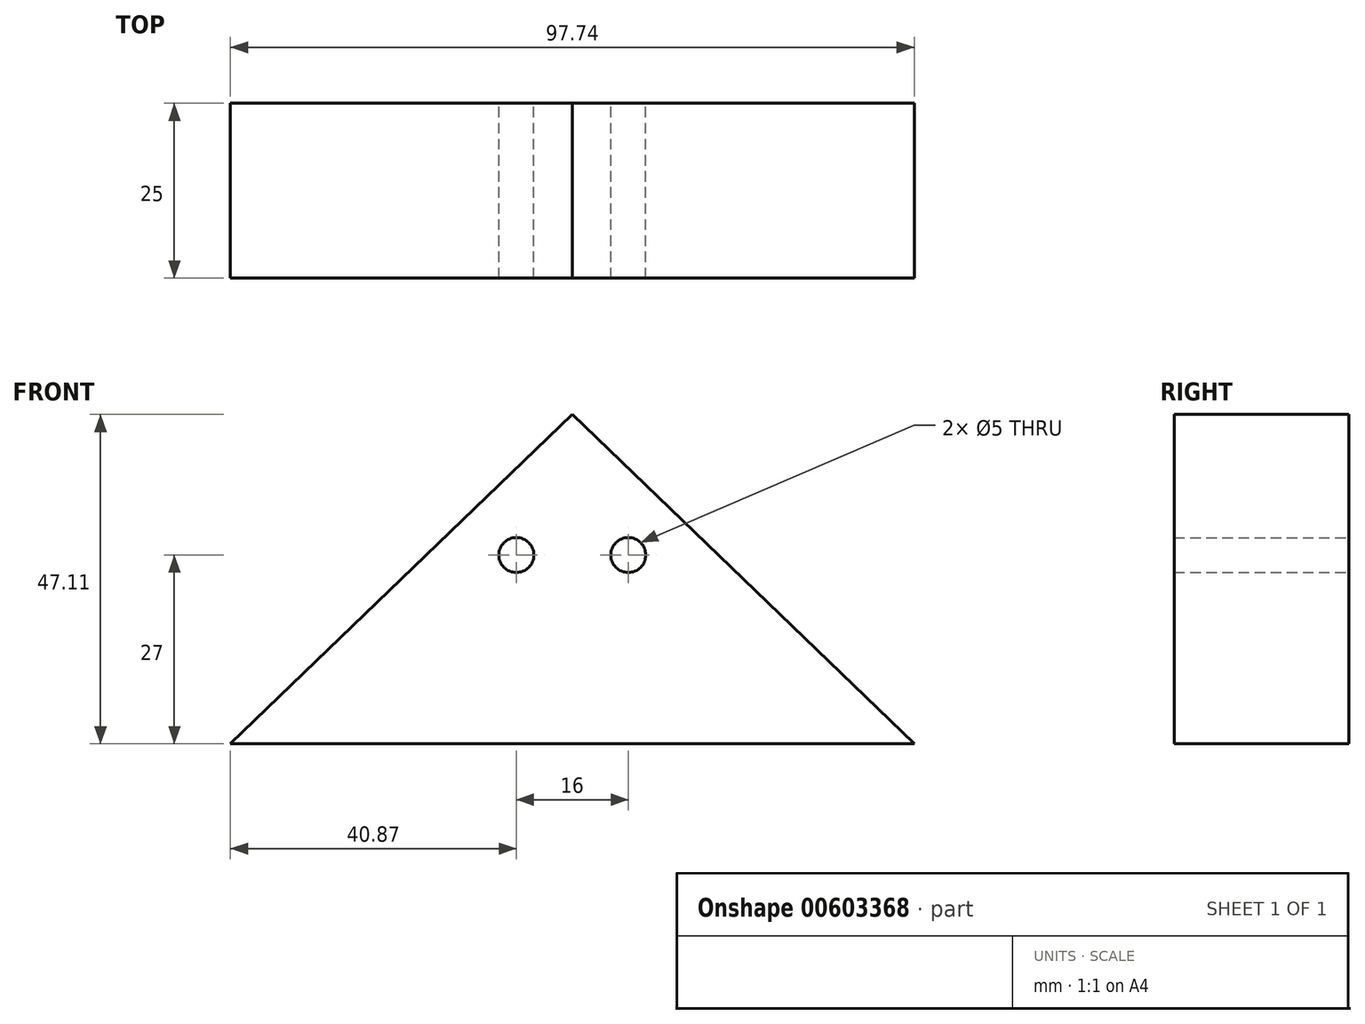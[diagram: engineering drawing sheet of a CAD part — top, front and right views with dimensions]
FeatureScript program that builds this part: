
annotation { "Feature Type Name" : "Feature", "Feature Type Description" : "" }
export const myFeature = defineFeature(function(context is Context, id is Id, definition is map)
    precondition{}
    {
        {
            var Q0;
            Q0=qCreatedBy(makeId("Top.planeOp"),FACE);
            var sketch = newSketch(context, id + "F0", { "sketchPlane" : qUnion([Q0])});
            skLineSegment(sketch, "E0", {"start": v(-327.3, -140.86) * mm, "end": v(-102.6, -140.86) * mm});
            skLineSegment(sketch, "E1", {"start": v(-102.6, -140.86) * mm, "end": v(-102.6, -170.86) * mm});
            skLineSegment(sketch, "E2", {"start": v(-102.6, -170.86) * mm, "end": v(0, -170.86) * mm});
            skLineSegment(sketch, "E3", {"start": v(0, -170.86) * mm, "end": v(0, -140.86) * mm});
            skLineSegment(sketch, "E4", {"start": v(0, -140.86) * mm, "end": v(288.9, -140.86) * mm});
            skLineSegment(sketch, "E5", {"start": v(288.9, -140.86) * mm, "end": v(288.9, 108.14) * mm});
            skLineSegment(sketch, "E6", {"start": v(288.9, 108.14) * mm, "end": v(0, 108.14) * mm});
            skLineSegment(sketch, "E7", {"start": v(0, 108.14) * mm, "end": v(0, 138.14) * mm});
            skLineSegment(sketch, "E8", {"start": v(-102.6, 128.64) * mm, "end": v(-102.6, 108.14) * mm});
            skLineSegment(sketch, "E9", {"start": v(-102.6, 108.14) * mm, "end": v(-327.3, 108.14) * mm});
            skLineSegment(sketch, "E10", {"start": v(-327.3, 108.14) * mm, "end": v(-327.3, -140.86) * mm});
            skLineSegment(sketch, "E11", {"start": v(-102.6, 128.64) * mm, "end": v(0, 138.14) * mm});
            skSolve(sketch);
        }
        {
            var Q0;
            Q0=makeQuery(id+"F0.imprint","IMPRINT",FACE,{"disambiguationData":[TD([[makeQuery(id+"F0.imprint","IMPRINT",EDGE,{"derivedFrom":sQuery(id+"F0.wireOp",EDGE,"E0")}),1.0]])]});
            extrude(context, id + "F1", {"entities" : qUnion([Q0]), "depth" : 8 * mm, "offsetDistance" : 25 * mm});
        }
        {
            var Q0;
            Q0=makeQuery(id+"F1.opExtrude","SWEPT_FACE",FACE,{"disambiguationData":[OSD([sQuery(id+"F0.wireOp",EDGE,"E5")])]});
            var sketch = newSketch(context, id + "F2", { "sketchPlane" : qUnion([Q0])});
            skLineSegment(sketch, "E12", {"start": v(-146.36, 8) * mm, "end": v(113.64, 8) * mm});
            skPoint(sketch, "E13", {"position": v(-140.86, 8) * mm});
            skPoint(sketch, "E14", {"position": v(108.14, 8) * mm});
            skLineSegment(sketch, "E15", {"start": v(-146.36, 8) * mm, "end": v(-16.36, 51.45) * mm});
            skLineSegment(sketch, "E16", {"start": v(-16.36, 51.45) * mm, "end": v(113.64, 8) * mm});
            skPoint(sketch, "E17", {"position": v(-16.36, 8) * mm});
            skSolve(sketch);
        }
        {
            var Q0;
            {var subQ0=sQuery(id+"F2.wireOp",EDGE,"E15");Q0=makeQuery(id+"F2.imprint","IMPRINT",FACE,{"disambiguationData":[TD([[makeQuery(id+"F2.imprint","IMPRINT",EDGE,{"derivedFrom":subQ0}),-1.0]])]});}
            extrude(context, id + "F3", {"entities" : qUnion([Q0]), "operationType" : NewBodyOperationType.ADD, "oppositeDirection" : true, "depth" : (616.2 + 5.5) * mm, "offsetDistance" : 25 * mm});
        }
        {
            var Q0;
            Q0=qSketchRegion(id+"F2",true);
            extrude(context, id + "F4", {"entities" : qUnion([Q0]), "operationType" : NewBodyOperationType.ADD, "depth" : 5.5 * mm, "offsetDistance" : 25 * mm});
        }
        {
            var Q0;
            Q0=makeQuery(id+"F1.opExtrude","SWEPT_FACE",FACE,{"disambiguationData":[OSD([sQuery(id+"F0.wireOp",EDGE,"E2")])]});
            var sketch = newSketch(context, id + "F5", { "sketchPlane" : qUnion([Q0])});
            skLineSegment(sketch, "E18", {"start": v(-108.1, 8) * mm, "end": v(5.5, 8) * mm});
            skPoint(sketch, "E19", {"position": v(-102.6, 8) * mm});
            skPoint(sketch, "E20", {"position": v(0, 8) * mm});
            skPoint(sketch, "E21", {"position": v(-51.3, 8) * mm});
            skLineSegment(sketch, "E22", {"start": v(-51.3, 8) * mm, "end": v(-51.3, 90.85) * mm, "construction": true});
            skPoint(sketch, "E23", {"position": v(-51.3, 62.75) * mm});
            skLineSegment(sketch, "E24", {"start": v(-108.1, 8) * mm, "end": v(-51.3, 62.75) * mm});
            skLineSegment(sketch, "E25", {"start": v(-51.3, 62.75) * mm, "end": v(5.5, 8) * mm});
            skSolve(sketch);
        }
        {
            var Q0;
            Q0=qSketchRegion(id+"F5",true);
            var Q1;
            Q1=makeQuery(id+"F1.opExtrude","SWEPT_FACE",FACE,{"disambiguationData":[OSD([sQuery(id+"F0.wireOp",EDGE,"E11")])]});
            extrude(context, id + "F6", {"entities" : qUnion([Q0]), "operationType" : NewBodyOperationType.ADD, "endBound" : BoundingType.UP_TO_SURFACE, "oppositeDirection" : true, "depth" : 25 * mm, "endBoundEntityFace" : qUnion([Q1]), "hasOffset" : true, "offsetDistance" : -5.5 * mm});
        }
        {
            var Q0;
            Q0=qSketchRegion(id+"F5",true);
            extrude(context, id + "F7", {"entities" : qUnion([Q0]), "operationType" : NewBodyOperationType.ADD, "depth" : 5.5 * mm, "offsetDistance" : 25 * mm});
        }
        {
            var Q0;
            Q0=makeQuery(id+"F6.opExtrude","CAP_FACE",FACE,{"disambiguationData":[OSD([sQuery(id+"F5.wireOp",EDGE,"E18"),sQuery(id+"F5.wireOp",EDGE,"E24"),sQuery(id+"F5.wireOp",EDGE,"E25")])],"isStart":false});
            var sketch = newSketch(context, id + "F8", { "sketchPlane" : qUnion([Q0])});
            skLineSegment(sketch, "E26.0", {"start": v(38.28, 55.82) * mm, "end": v(-15.3, 4.4) * mm});
            skLineSegment(sketch, "E26.1", {"start": v(91.86, 4.4) * mm, "end": v(38.28, 55.82) * mm});
            skLineSegment(sketch, "E27", {"start": v(-15.3, 4.4) * mm, "end": v(91.86, 4.4) * mm});
            skSolve(sketch);
        }
        {
            var Q0;
            {var subQ0=sQuery(id+"F8.wireOp",EDGE,"E26.1");var subQ1=sQuery(id+"F8.wireOp",EDGE,"E26.0");var subQ2=makeQuery(id+"F8.imprint","INTERSECT",VERTEX,{"derivedFrom":[subQ1,subQ0]});Q0=makeQuery(id+"F8.imprint","IMPRINT",FACE,{"disambiguationData":[TD([[makeQuery(id+"F8.imprint","IMPRINT",EDGE,{"disambiguationData":[TD([[subQ2,-1.0]])],"derivedFrom":subQ1}),1.0]])]});}
            extrude(context, id + "F9", {"entities" : qUnion([Q0]), "operationType" : NewBodyOperationType.REMOVE, "oppositeDirection" : true, "depth" : 5.5 * mm, "offsetDistance" : 25 * mm});
        }
        {
            var Q0;
            Q0=makeQuery(id+"F3.opExtrude","CAP_FACE",FACE,{"disambiguationData":[OSD([sQuery(id+"F2.wireOp",EDGE,"E12"),sQuery(id+"F2.wireOp",EDGE,"E15"),sQuery(id+"F2.wireOp",EDGE,"E16")])],"isStart":false});
            var sketch = newSketch(context, id + "F10", { "sketchPlane" : qUnion([Q0])});
            skLineSegment(sketch, "E28.0", {"start": v(16.36, 45.65) * mm, "end": v(-111.9, 2.78) * mm});
            skLineSegment(sketch, "E28.1", {"start": v(144.61, 2.78) * mm, "end": v(16.36, 45.65) * mm});
            skLineSegment(sketch, "E29", {"start": v(-111.9, 2.78) * mm, "end": v(144.61, 2.78) * mm});
            skSolve(sketch);
        }
        {
            var Q0;
            Q0=qSketchRegion(id+"F10",true);
            extrude(context, id + "F11", {"entities" : qUnion([Q0]), "operationType" : NewBodyOperationType.REMOVE, "oppositeDirection" : true, "depth" : 5.5 * mm, "offsetDistance" : 25 * mm});
        }
        {
            var Q0;
            Q0=makeQuery(id+"F4.opExtrude","CAP_FACE",FACE,{"disambiguationData":[OSD([sQuery(id+"F2.wireOp",EDGE,"E12"),sQuery(id+"F2.wireOp",EDGE,"E15"),sQuery(id+"F2.wireOp",EDGE,"E16")])],"isStart":false});
            var sketch = newSketch(context, id + "F12", { "sketchPlane" : qUnion([Q0])});
            skLineSegment(sketch, "E30.0", {"start": v(-16.36, 45.65) * mm, "end": v(111.9, 2.78) * mm});
            skLineSegment(sketch, "E30.1", {"start": v(-144.61, 2.78) * mm, "end": v(-16.36, 45.65) * mm});
            skLineSegment(sketch, "E31", {"start": v(-144.61, 2.78) * mm, "end": v(111.9, 2.78) * mm});
            skSolve(sketch);
        }
        {
            var Q0;
            Q0=qSketchRegion(id+"F12",true);
            extrude(context, id + "F13", {"entities" : qUnion([Q0]), "operationType" : NewBodyOperationType.REMOVE, "oppositeDirection" : true, "depth" : 5.5 * mm, "offsetDistance" : 25 * mm});
        }
        {
            var Q0;
            Q0=makeQuery(id+"F7.opExtrude","CAP_FACE",FACE,{"disambiguationData":[OSD([sQuery(id+"F5.wireOp",EDGE,"E18"),sQuery(id+"F5.wireOp",EDGE,"E24"),sQuery(id+"F5.wireOp",EDGE,"E25")])],"isStart":false});
            var sketch = newSketch(context, id + "F14", { "sketchPlane" : qUnion([Q0])});
            skLineSegment(sketch, "E32.0", {"start": v(-51.3, 55.11) * mm, "end": v(1.68, 4.04) * mm});
            skLineSegment(sketch, "E32.1", {"start": v(-104.28, 4.04) * mm, "end": v(-51.3, 55.11) * mm});
            skLineSegment(sketch, "E33", {"start": v(-104.28, 4.04) * mm, "end": v(1.68, 4.04) * mm});
            skSolve(sketch);
        }
        {
            var Q0;
            Q0=qSketchRegion(id+"F14",true);
            extrude(context, id + "F15", {"entities" : qUnion([Q0]), "operationType" : NewBodyOperationType.REMOVE, "oppositeDirection" : true, "depth" : 5.5 * mm, "offsetDistance" : 25 * mm});
        }
        {
            var Q0;
            Q0=makeQuery(id+"F4.opExtrude","CAP_FACE",FACE,{"disambiguationData":[OSD([sQuery(id+"F2.wireOp",EDGE,"E12"),sQuery(id+"F2.wireOp",EDGE,"E15"),sQuery(id+"F2.wireOp",EDGE,"E16")])],"isStart":false});
            var sketch = newSketch(context, id + "F16", { "sketchPlane" : qUnion([Q0])});
            skLineSegment(sketch, "E34", {"start": v(-36.64, 44.67) * mm, "end": v(-16.36, 51.45) * mm});
            skLineSegment(sketch, "E35", {"start": v(-16.36, 51.45) * mm, "end": v(3.93, 44.67) * mm});
            skLineSegment(sketch, "E36.0", {"start": v(-16.36, 55.67) * mm, "end": v(5.2, 48.47) * mm});
            skLineSegment(sketch, "E36.1", {"start": v(-37.91, 48.47) * mm, "end": v(-16.36, 55.67) * mm});
            skLineSegment(sketch, "E37", {"start": v(-37.91, 48.47) * mm, "end": v(-36.64, 44.67) * mm});
            skLineSegment(sketch, "E38", {"start": v(5.2, 48.47) * mm, "end": v(3.93, 44.67) * mm});
            skSolve(sketch);
        }
        {
            var Q0;
            Q0=makeQuery(id+"F16.imprint","IMPRINT",FACE,{"disambiguationData":[TD([[makeQuery(id+"F16.imprint","IMPRINT",EDGE,{"derivedFrom":sQuery(id+"F16.wireOp",EDGE,"E34")}),1.0]])]});
            extrude(context, id + "F17", {"entities" : qUnion([Q0]), "operationType" : NewBodyOperationType.ADD, "oppositeDirection" : true, "depth" : (30.35 + 277.85) * mm, "offsetDistance" : 25 * mm});
        }
        {
            var Q0;
            Q0=qSketchRegion(id+"F16",true);
            extrude(context, id + "F18", {"entities" : qUnion([Q0]), "operationType" : NewBodyOperationType.REMOVE, "oppositeDirection" : true, "depth" : 24 * mm, "offsetDistance" : 25 * mm});
        }
        {
            var Q0;
            Q0=makeQuery(id+"F3.opExtrude","CAP_FACE",FACE,{"disambiguationData":[OSD([sQuery(id+"F2.wireOp",EDGE,"E12"),sQuery(id+"F2.wireOp",EDGE,"E15"),sQuery(id+"F2.wireOp",EDGE,"E16")])],"isStart":false});
            var sketch = newSketch(context, id + "F19", { "sketchPlane" : qUnion([Q0])});
            skLineSegment(sketch, "E39", {"start": v(-3.93, 44.67) * mm, "end": v(16.36, 51.45) * mm});
            skLineSegment(sketch, "E40", {"start": v(16.36, 51.45) * mm, "end": v(36.64, 44.67) * mm});
            skLineSegment(sketch, "E41.0", {"start": v(16.36, 55.67) * mm, "end": v(37.91, 48.47) * mm});
            skLineSegment(sketch, "E41.1", {"start": v(-5.2, 48.47) * mm, "end": v(16.36, 55.67) * mm});
            skLineSegment(sketch, "E42", {"start": v(-5.2, 48.47) * mm, "end": v(-3.93, 44.67) * mm});
            skLineSegment(sketch, "E43", {"start": v(37.91, 48.47) * mm, "end": v(36.64, 44.67) * mm});
            skSolve(sketch);
        }
        {
            var Q0;
            Q0=qSketchRegion(id+"F19",true);
            extrude(context, id + "F20", {"entities" : qUnion([Q0]), "operationType" : NewBodyOperationType.ADD, "oppositeDirection" : true, "depth" : (30.35 + 213.85) * mm, "offsetDistance" : 25 * mm});
        }
        {
            var Q0;
            Q0=qSketchRegion(id+"F19",true);
            extrude(context, id + "F21", {"entities" : qUnion([Q0]), "operationType" : NewBodyOperationType.REMOVE, "oppositeDirection" : true, "depth" : 30.35 * mm, "offsetDistance" : 25 * mm});
        }
        {
            var Q0;
            Q0=makeQuery(id+"F11.boolean.opBoolean","MERGE",FACE,{"derivedFrom":[makeQuery(id+"F1.opExtrude","SWEPT_FACE",FACE,{"disambiguationData":[OSD([sQuery(id+"F0.wireOp",EDGE,"E10")])]}),makeQuery(id+"F11.opExtrude","CAP_FACE",FACE,{"disambiguationData":[OSD([sQuery(id+"F10.wireOp",EDGE,"E28.0"),sQuery(id+"F10.wireOp",EDGE,"E28.1"),sQuery(id+"F10.wireOp",EDGE,"E29")])],"isStart":false})]});
            var sketch = newSketch(context, id + "F22", { "sketchPlane" : qUnion([Q0])});
            skPoint(sketch, "E44", {"position": v(16.36, 0) * mm});
            skLineSegment(sketch, "E45", {"start": v(16.36, 0) * mm, "end": v(16.36, 35) * mm, "construction": true});
            skLineSegment(sketch, "E46", {"start": v(-4.2, 35) * mm, "end": v(35.76, 35) * mm, "construction": true});
            skPoint(sketch, "E47", {"position": v(8.36, 35) * mm});
            skPoint(sketch, "E48", {"position": v(24.36, 35) * mm});
            skCircle(sketch, "E49", {"center": v(8.36, 35) * mm, "radius": 2.5 * mm});
            skCircle(sketch, "E50", {"center": v(24.36, 35) * mm, "radius": 2.5 * mm});
            skSolve(sketch);
        }
        {
            var Q0;
            Q0=qSketchRegion(id+"F22",true);
            extrude(context, id + "F23", {"entities" : qUnion([Q0]), "operationType" : NewBodyOperationType.REMOVE, "oppositeDirection" : true, "depth" : .5 * mm, "offsetDistance" : 25 * mm});
        }
        {
            var Q0;
            Q0=makeQuery(id+"F13.boolean.opBoolean","MERGE",FACE,{"derivedFrom":[makeQuery(id+"F3.boolean.opBoolean","MERGE",FACE,{"derivedFrom":[makeQuery(id+"F1.opExtrude","SWEPT_FACE",FACE,{"disambiguationData":[OSD([sQuery(id+"F0.wireOp",EDGE,"E5")])]}),makeQuery(id+"F3.opExtrude","CAP_FACE",FACE,{"disambiguationData":[OSD([sQuery(id+"F2.wireOp",EDGE,"E12"),sQuery(id+"F2.wireOp",EDGE,"E15"),sQuery(id+"F2.wireOp",EDGE,"E16")])],"isStart":true})]}),makeQuery(id+"F13.opExtrude","CAP_FACE",FACE,{"disambiguationData":[OSD([sQuery(id+"F12.wireOp",EDGE,"E30.0"),sQuery(id+"F12.wireOp",EDGE,"E30.1"),sQuery(id+"F12.wireOp",EDGE,"E31")])],"isStart":false})]});
            var sketch = newSketch(context, id + "F24", { "sketchPlane" : qUnion([Q0])});
            skPoint(sketch, "E51", {"position": v(-16.36, 0) * mm});
            skLineSegment(sketch, "E52", {"start": v(-16.36, 0) * mm, "end": v(-16.36, 35) * mm, "construction": true});
            skLineSegment(sketch, "E53", {"start": v(-48.45, 35) * mm, "end": v(-8.49, 35) * mm, "construction": true});
            skPoint(sketch, "E54", {"position": v(-24.36, 35) * mm});
            skPoint(sketch, "E55", {"position": v(-8.36, 35) * mm});
            skCircle(sketch, "E56", {"center": v(-24.36, 35) * mm, "radius": 2.5 * mm});
            skCircle(sketch, "E57", {"center": v(-8.36, 35) * mm, "radius": 2.5 * mm});
            skSolve(sketch);
        }
        {
            var Q0;
            Q0=qSketchRegion(id+"F24",true);
            extrude(context, id + "F25", {"entities" : qUnion([Q0]), "operationType" : NewBodyOperationType.REMOVE, "oppositeDirection" : true, "depth" : .5 * mm, "offsetDistance" : 25 * mm});
        }
        {
            var Q0;
            Q0=makeQuery(id+"F15.boolean.opBoolean","MERGE",FACE,{"derivedFrom":[makeQuery(id+"F6.boolean.opBoolean","MERGE",FACE,{"derivedFrom":[makeQuery(id+"F1.opExtrude","SWEPT_FACE",FACE,{"disambiguationData":[OSD([sQuery(id+"F0.wireOp",EDGE,"E2")])]}),makeQuery(id+"F6.opExtrude","CAP_FACE",FACE,{"disambiguationData":[OSD([sQuery(id+"F5.wireOp",EDGE,"E18"),sQuery(id+"F5.wireOp",EDGE,"E24"),sQuery(id+"F5.wireOp",EDGE,"E25")])],"isStart":true})]})],"fromTools":[makeQuery(id+"F15.opExtrude","CAP_FACE",FACE,{"disambiguationData":[OSD([sQuery(id+"F14.wireOp",EDGE,"E32.0"),sQuery(id+"F14.wireOp",EDGE,"E32.1"),sQuery(id+"F14.wireOp",EDGE,"E33")])],"isStart":false})]});
            var sketch = newSketch(context, id + "F26", { "sketchPlane" : qUnion([Q0])});
            skPoint(sketch, "E58", {"position": v(-51.3, 0) * mm});
            skLineSegment(sketch, "E59", {"start": v(-51.3, 0) * mm, "end": v(-51.3, 35) * mm, "construction": true});
            skLineSegment(sketch, "E60", {"start": v(-73.66, 35) * mm, "end": v(-33.7, 35) * mm, "construction": true});
            skPoint(sketch, "E61", {"position": v(-59.3, 35) * mm});
            skPoint(sketch, "E62", {"position": v(-43.3, 35) * mm});
            skCircle(sketch, "E63", {"center": v(-59.3, 35) * mm, "radius": 2.5 * mm});
            skCircle(sketch, "E64", {"center": v(-43.3, 35) * mm, "radius": 2.5 * mm});
            skSolve(sketch);
        }
        {
            var Q0;
            Q0=qSketchRegion(id+"F26",true);
            extrude(context, id + "F27", {"entities" : qUnion([Q0]), "operationType" : NewBodyOperationType.REMOVE, "oppositeDirection" : true, "depth" : .5 * mm, "offsetDistance" : 25 * mm});
        }
        {
            var Q0;
            Q0=makeQuery(id+"F1.opExtrude","SWEPT_FACE",FACE,{"disambiguationData":[OSD([sQuery(id+"F0.wireOp",EDGE,"E11")])]});
            var sketch = newSketch(context, id + "F28", { "sketchPlane" : qUnion([Q0])});
            skPoint(sketch, "E65", {"position": v(38.78, 0) * mm});
            skLineSegment(sketch, "E66", {"start": v(38.78, 0) * mm, "end": v(38.78, 35) * mm, "construction": true});
            skLineSegment(sketch, "E67", {"start": v(13.04, 35) * mm, "end": v(53, 35) * mm, "construction": true});
            skPoint(sketch, "E68", {"position": v(30.78, 35) * mm});
            skPoint(sketch, "E69", {"position": v(46.78, 35) * mm});
            skCircle(sketch, "E70", {"center": v(30.78, 35) * mm, "radius": 2.5 * mm});
            skCircle(sketch, "E71", {"center": v(46.78, 35) * mm, "radius": 2.5 * mm});
            skSolve(sketch);
        }
        {
            var Q0;
            Q0=qSketchRegion(id+"F28",true);
            extrude(context, id + "F29", {"entities" : qUnion([Q0]), "operationType" : NewBodyOperationType.REMOVE, "oppositeDirection" : true, "depth" : .5 * mm, "offsetDistance" : 25 * mm});
        }
        {
            var Q0;
            Q0=makeQuery(id+"F13.boolean.opBoolean","MERGE",FACE,{"derivedFrom":[makeQuery(id+"F3.boolean.opBoolean","MERGE",FACE,{"derivedFrom":[makeQuery(id+"F1.opExtrude","SWEPT_FACE",FACE,{"disambiguationData":[OSD([sQuery(id+"F0.wireOp",EDGE,"E5")])]}),makeQuery(id+"F3.opExtrude","CAP_FACE",FACE,{"disambiguationData":[OSD([sQuery(id+"F2.wireOp",EDGE,"E12"),sQuery(id+"F2.wireOp",EDGE,"E15"),sQuery(id+"F2.wireOp",EDGE,"E16")])],"isStart":true})]}),makeQuery(id+"F13.opExtrude","CAP_FACE",FACE,{"disambiguationData":[OSD([sQuery(id+"F12.wireOp",EDGE,"E30.0"),sQuery(id+"F12.wireOp",EDGE,"E30.1"),sQuery(id+"F12.wireOp",EDGE,"E31")])],"isStart":false})]});
            var sketch = newSketch(context, id + "F30", { "sketchPlane" : qUnion([Q0])});
            skPoint(sketch, "E72", {"position": v(-16.36, 0) * mm});
            skLineSegment(sketch, "E73", {"start": v(-16.36, 0) * mm, "end": v(-16.36, 40.85) * mm, "construction": true});
            skLineSegment(sketch, "E74.bottom", {"start": v(-23.43, 23) * mm, "end": v(-9.29, 23) * mm});
            skLineSegment(sketch, "E74.top", {"start": v(-23.43, 5) * mm, "end": v(-9.29, 5) * mm});
            skLineSegment(sketch, "E74.left", {"start": v(-23.43, 23) * mm, "end": v(-23.43, 5) * mm});
            skLineSegment(sketch, "E74.right", {"start": v(-9.29, 23) * mm, "end": v(-9.29, 5) * mm});
            skLineSegment(sketch, "E75.0", {"start": v(-21.5, 21.07) * mm, "end": v(-17.32, 21.07) * mm});
            skLineSegment(sketch, "E75.1", {"start": v(-21.5, 21.07) * mm, "end": v(-21.5, 14.96) * mm});
            skLineSegment(sketch, "E75.2", {"start": v(-21.5, 6.93) * mm, "end": v(-17.32, 6.93) * mm});
            skLineSegment(sketch, "E75.3", {"start": v(-11.21, 21.07) * mm, "end": v(-11.21, 14.96) * mm});
            skLineSegment(sketch, "E76.left", {"start": v(-17.32, 21.07) * mm, "end": v(-17.32, 14.96) * mm});
            skLineSegment(sketch, "E76.right", {"start": v(-15.4, 21.07) * mm, "end": v(-15.4, 14.96) * mm});
            skLineSegment(sketch, "E77.bottom", {"start": v(-11.21, 14.96) * mm, "end": v(-15.4, 14.96) * mm});
            skLineSegment(sketch, "E77.top", {"start": v(-11.21, 13.04) * mm, "end": v(-15.4, 13.04) * mm});
            skLineSegment(sketch, "E78.trimOffspring", {"start": v(-17.32, 14.96) * mm, "end": v(-21.5, 14.96) * mm});
            skLineSegment(sketch, "E79.trimOffspring", {"start": v(-17.32, 13.04) * mm, "end": v(-17.32, 6.93) * mm});
            skLineSegment(sketch, "E80.trimOffspring", {"start": v(-17.32, 13.04) * mm, "end": v(-21.5, 13.04) * mm});
            skLineSegment(sketch, "E81.trimOffspring", {"start": v(-15.4, 13.04) * mm, "end": v(-15.4, 6.93) * mm});
            skLineSegment(sketch, "E82.trimOffspring", {"start": v(-11.21, 13.04) * mm, "end": v(-11.21, 6.93) * mm});
            skLineSegment(sketch, "E83.trimOffspring", {"start": v(-21.5, 13.04) * mm, "end": v(-21.5, 6.93) * mm});
            skLineSegment(sketch, "E84.trimOffspring", {"start": v(-15.4, 21.07) * mm, "end": v(-11.21, 21.07) * mm});
            skLineSegment(sketch, "E85.trimOffspring", {"start": v(-15.4, 6.93) * mm, "end": v(-11.21, 6.93) * mm});
            skPoint(sketch, "E86", {"position": v(-16.36, 23) * mm});
            skLineSegment(sketch, "E87.1.0.0", {"start": v(19.6, 13.04) * mm, "end": v(19.6, 6.93) * mm});
            skPoint(sketch, "E87.1.0.1", {"position": v(18.64, 23) * mm});
            skLineSegment(sketch, "E87.1.0.2", {"start": v(19.6, 6.93) * mm, "end": v(23.79, 6.93) * mm});
            skLineSegment(sketch, "E87.1.0.3", {"start": v(13.5, 13.04) * mm, "end": v(13.5, 6.93) * mm});
            skLineSegment(sketch, "E87.1.0.4", {"start": v(17.68, 13.04) * mm, "end": v(17.68, 6.93) * mm});
            skLineSegment(sketch, "E87.1.0.5", {"start": v(11.57, 5) * mm, "end": v(25.71, 5) * mm});
            skLineSegment(sketch, "E87.1.0.6", {"start": v(11.57, 23) * mm, "end": v(25.71, 23) * mm});
            skLineSegment(sketch, "E87.1.0.7", {"start": v(25.71, 23) * mm, "end": v(25.71, 5) * mm});
            skLineSegment(sketch, "E87.1.0.8", {"start": v(11.57, 23) * mm, "end": v(11.57, 5) * mm});
            skLineSegment(sketch, "E87.1.0.9", {"start": v(23.79, 13.04) * mm, "end": v(23.79, 6.93) * mm});
            skLineSegment(sketch, "E87.1.0.10", {"start": v(23.79, 13.04) * mm, "end": v(19.6, 13.04) * mm});
            skLineSegment(sketch, "E87.1.0.11", {"start": v(17.68, 21.07) * mm, "end": v(17.68, 14.96) * mm});
            skLineSegment(sketch, "E87.1.0.12", {"start": v(13.5, 21.07) * mm, "end": v(17.68, 21.07) * mm});
            skLineSegment(sketch, "E87.1.0.13", {"start": v(19.6, 21.07) * mm, "end": v(19.6, 14.96) * mm});
            skLineSegment(sketch, "E87.1.0.14", {"start": v(13.5, 6.93) * mm, "end": v(17.68, 6.93) * mm});
            skLineSegment(sketch, "E87.1.0.15", {"start": v(23.79, 21.07) * mm, "end": v(23.79, 14.96) * mm});
            skLineSegment(sketch, "E87.1.0.16", {"start": v(17.68, 13.04) * mm, "end": v(13.5, 13.04) * mm});
            skLineSegment(sketch, "E87.1.0.17", {"start": v(17.68, 14.96) * mm, "end": v(13.5, 14.96) * mm});
            skLineSegment(sketch, "E87.1.0.18", {"start": v(23.79, 14.96) * mm, "end": v(19.6, 14.96) * mm});
            skLineSegment(sketch, "E87.1.0.19", {"start": v(19.6, 21.07) * mm, "end": v(23.79, 21.07) * mm});
            skLineSegment(sketch, "E87.1.0.20", {"start": v(13.5, 21.07) * mm, "end": v(13.5, 14.96) * mm});
            skLineSegment(sketch, "E87.direction1", {"start": v(-23.43, 5) * mm, "end": v(11.57, 5) * mm, "construction": true});
            skLineSegment(sketch, "E88.1.0.0", {"start": v(-50.4, 6.93) * mm, "end": v(-46.21, 6.93) * mm});
            skPoint(sketch, "E88.1.0.1", {"position": v(-51.36, 0) * mm});
            skLineSegment(sketch, "E88.1.0.2", {"start": v(-58.43, 5) * mm, "end": v(-44.29, 5) * mm});
            skLineSegment(sketch, "E88.1.0.3", {"start": v(-44.29, 23) * mm, "end": v(-44.29, 5) * mm});
            skLineSegment(sketch, "E88.1.0.4", {"start": v(-58.43, 23) * mm, "end": v(-58.43, 5) * mm});
            skLineSegment(sketch, "E88.1.0.5", {"start": v(-46.21, 21.07) * mm, "end": v(-46.21, 14.96) * mm});
            skLineSegment(sketch, "E88.1.0.6", {"start": v(-56.5, 6.93) * mm, "end": v(-52.32, 6.93) * mm});
            skPoint(sketch, "E88.1.0.7", {"position": v(-51.36, 23) * mm});
            skLineSegment(sketch, "E88.1.0.8", {"start": v(-50.4, 13.04) * mm, "end": v(-50.4, 6.93) * mm});
            skLineSegment(sketch, "E88.1.0.9", {"start": v(-52.32, 13.04) * mm, "end": v(-56.5, 13.04) * mm});
            skLineSegment(sketch, "E88.1.0.10", {"start": v(-52.32, 13.04) * mm, "end": v(-52.32, 6.93) * mm});
            skLineSegment(sketch, "E88.1.0.11", {"start": v(-58.43, 23) * mm, "end": v(-44.29, 23) * mm});
            skLineSegment(sketch, "E88.1.0.12", {"start": v(-52.32, 14.96) * mm, "end": v(-56.5, 14.96) * mm});
            skLineSegment(sketch, "E88.1.0.13", {"start": v(-46.21, 13.04) * mm, "end": v(-50.4, 13.04) * mm});
            skLineSegment(sketch, "E88.1.0.14", {"start": v(-46.21, 14.96) * mm, "end": v(-50.4, 14.96) * mm});
            skLineSegment(sketch, "E88.1.0.15", {"start": v(-50.4, 21.07) * mm, "end": v(-46.21, 21.07) * mm});
            skLineSegment(sketch, "E88.1.0.16", {"start": v(-56.5, 21.07) * mm, "end": v(-56.5, 14.96) * mm});
            skLineSegment(sketch, "E88.1.0.17", {"start": v(-56.5, 21.07) * mm, "end": v(-52.32, 21.07) * mm});
            skLineSegment(sketch, "E88.1.0.18", {"start": v(-50.4, 21.07) * mm, "end": v(-50.4, 14.96) * mm});
            skLineSegment(sketch, "E88.1.0.19", {"start": v(-52.32, 21.07) * mm, "end": v(-52.32, 14.96) * mm});
            skLineSegment(sketch, "E88.1.0.20", {"start": v(-56.5, 13.04) * mm, "end": v(-56.5, 6.93) * mm});
            skLineSegment(sketch, "E88.1.0.21", {"start": v(-46.21, 13.04) * mm, "end": v(-46.21, 6.93) * mm});
            skLineSegment(sketch, "E88.direction1", {"start": v(-23.43, 5) * mm, "end": v(-58.43, 5) * mm, "construction": true});
            skSolve(sketch);
        }
        {
            var Q0;
            Q0=qSketchRegion(id+"F30",true);
            extrude(context, id + "F31", {"entities" : qUnion([Q0]), "operationType" : NewBodyOperationType.REMOVE, "oppositeDirection" : true, "depth" : 0.5 * mm, "offsetDistance" : 25 * mm});
        }
        {
            var Q0;
            Q0=makeQuery(id+"F15.boolean.opBoolean","MERGE",FACE,{"derivedFrom":[makeQuery(id+"F6.boolean.opBoolean","MERGE",FACE,{"derivedFrom":[makeQuery(id+"F1.opExtrude","SWEPT_FACE",FACE,{"disambiguationData":[OSD([sQuery(id+"F0.wireOp",EDGE,"E2")])]}),makeQuery(id+"F6.opExtrude","CAP_FACE",FACE,{"disambiguationData":[OSD([sQuery(id+"F5.wireOp",EDGE,"E18"),sQuery(id+"F5.wireOp",EDGE,"E24"),sQuery(id+"F5.wireOp",EDGE,"E25")])],"isStart":true})]})],"fromTools":[makeQuery(id+"F15.opExtrude","CAP_FACE",FACE,{"disambiguationData":[OSD([sQuery(id+"F14.wireOp",EDGE,"E32.0"),sQuery(id+"F14.wireOp",EDGE,"E32.1"),sQuery(id+"F14.wireOp",EDGE,"E33")])],"isStart":false})]});
            extrude(context, id + "F32", {"entities" : qUnion([Q0]), "depth" : 25 * mm, "offsetDistance" : 25 * mm});
        }
        {
            var Q0;
            Q0=makeQuery(id+"F1.opExtrude","SWEPT_BODY",BODY,{"disambiguationData":[OSD([sQuery(id+"F0.wireOp",EDGE,"E0"),sQuery(id+"F0.wireOp",EDGE,"E1"),sQuery(id+"F0.wireOp",EDGE,"E2"),sQuery(id+"F0.wireOp",EDGE,"E3"),sQuery(id+"F0.wireOp",EDGE,"E4"),sQuery(id+"F0.wireOp",EDGE,"E5"),sQuery(id+"F0.wireOp",EDGE,"E6"),sQuery(id+"F0.wireOp",EDGE,"E7"),sQuery(id+"F0.wireOp",EDGE,"E8"),sQuery(id+"F0.wireOp",EDGE,"E9"),sQuery(id+"F0.wireOp",EDGE,"E10"),sQuery(id+"F0.wireOp",EDGE,"E11")])]});
            deleteBodies(context, id + "F33", {"entities" : qUnion([Q0])});
        }
        {
            var Q0;
            Q0=makeQuery(id+"F32.opExtrude","SWEPT_FACE",FACE,{"disambiguationData":[OSD([sQuery(id+"F0.wireOp",EDGE,"E2")])]});
            extrude(context, id + "F34", {"entities" : qUnion([Q0]), "operationType" : NewBodyOperationType.REMOVE, "oppositeDirection" : true, "depth" : 8 * mm, "offsetDistance" : 25 * mm});
        }
    });
